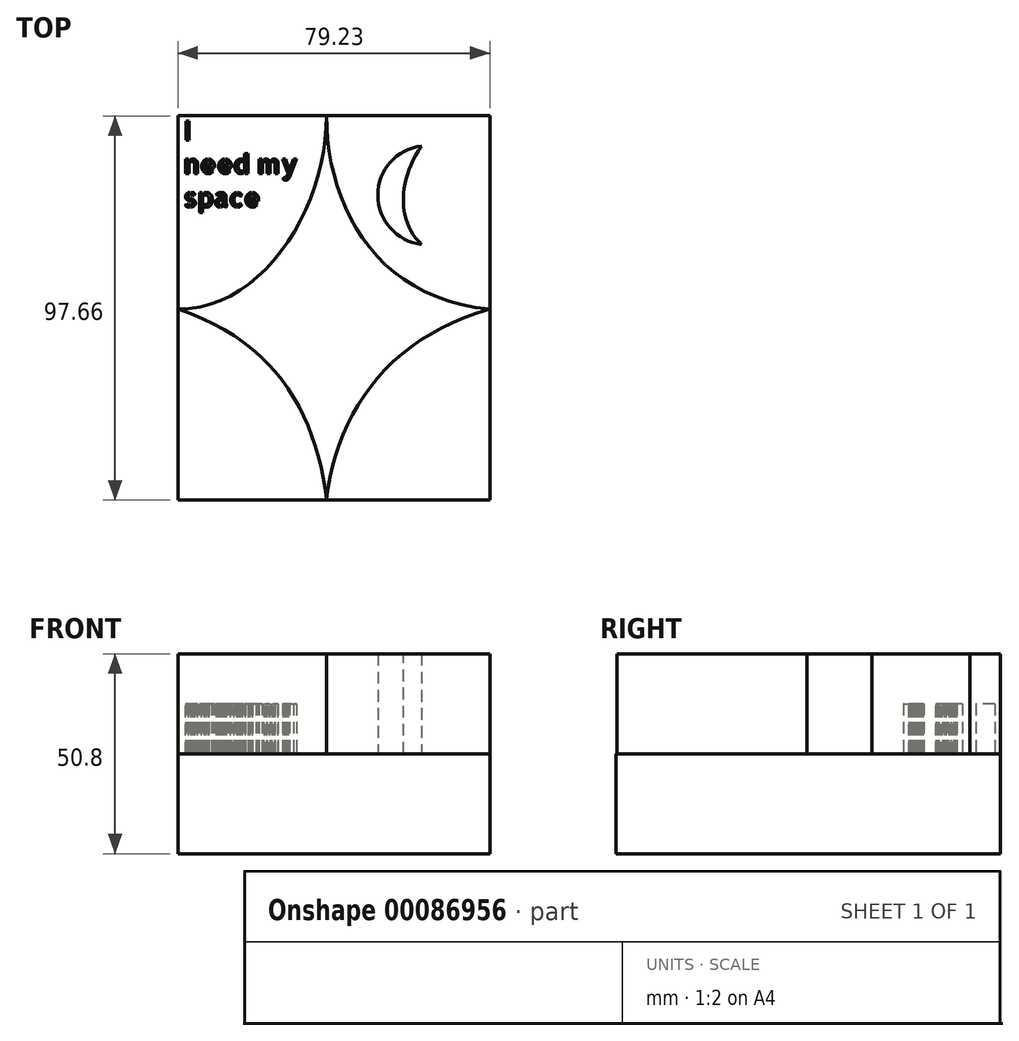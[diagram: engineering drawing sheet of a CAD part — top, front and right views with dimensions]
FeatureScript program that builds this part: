
annotation { "Feature Type Name" : "Feature", "Feature Type Description" : "" }
export const myFeature = defineFeature(function(context is Context, id is Id, definition is map)
    precondition{}
    {
        {
            var Q0;
            Q0=qCreatedBy(makeId("Top.planeOp"),FACE);
            var sketch = newSketch(context, id + "F0", { "sketchPlane" : qUnion([Q0])});
            skFitSpline(sketch, "E0", {"points": [v(-37.75, 0) * mm, v(0, 49.12) * mm], "startDerivative": vector(65.6, 0) * mm, "endDerivative": vector(-0.18, 69.09) * mm});
            skFitSpline(sketch, "E1", {"points": [v(0, 49.12) * mm, v(41.48, 0) * mm], "startDerivative": vector(0.18, -69.09) * mm, "endDerivative": vector(86.48, -7.94) * mm});
            skFitSpline(sketch, "E2", {"points": [v(41.48, 0) * mm, v(0, -48.24) * mm], "startDerivative": vector(-76.77, -21.18) * mm, "endDerivative": vector(-7.06, -65.3) * mm});
            skFitSpline(sketch, "E3", {"points": [v(-37.75, 0) * mm, v(0, -48.24) * mm], "startDerivative": vector(74.42, -24.7) * mm, "endDerivative": vector(7.94, -65.3) * mm});
            skLineSegment(sketch, "E4.bottom", {"start": v(-37.75, 49.12) * mm, "end": v(41.48, 49.12) * mm});
            skLineSegment(sketch, "E4.top", {"start": v(-37.75, -48.54) * mm, "end": v(41.48, -48.54) * mm});
            skLineSegment(sketch, "E4.left", {"start": v(-37.75, 49.12) * mm, "end": v(-37.75, -48.54) * mm});
            skLineSegment(sketch, "E4.right", {"start": v(41.48, 49.12) * mm, "end": v(41.48, -48.54) * mm});
            skSolve(sketch);
        }
        {
            var Q0;
            Q0=makeQuery(id+"F0.imprint","IMPRINT",FACE,{"disambiguationData":[TD([[makeQuery(id+"F0.imprint","IMPRINT",EDGE,{"derivedFrom":sQuery(id+"F0.wireOp",EDGE,"E0")}),-1.0]])]});
            extrude(context, id + "F1", {"entities" : qUnion([Q0]), "depth" : 50.8 * mm});
        }
        {
            var Q0;
            Q0 = qSketchRegion(id + "F0", true);
            extrude(context, id + "F2", {"entities" : qUnion([Q0]), "operationType" : NewBodyOperationType.ADD, "depth" : 25.4 * mm});
        }
        {
            var Q0;
            Q0=qCreatedBy(makeId("Top.planeOp"),FACE);
            var sketch = newSketch(context, id + "F3", { "sketchPlane" : qUnion([Q0])});
            skText(sketch, "E5", { "text": "I\nneed my\nspace", "fontName": "AllertaStencil-Regular.ttf"});
            const initialGuessF3  = {"E5": [-0.07133, 0.05854, 1, 0, 0.00478]};
            skSetInitialGuess(sketch, initialGuessF3);
            skSolve(sketch);
        }
        {
            var Q0;
            Q0 = qSketchRegion(id + "F3", true);
            extrude(context, id + "F4", {"entities" : qUnion([Q0]), "depth" : 12.7 * mm});
        }
        {
            var Q0;
            Q0=makeQuery(id+"F4.opExtrude","SWEPT_BODY",BODY,{"disambiguationData":[OSD([sQuery(id+"F3.wireOp",EDGE,"E5.sketch_text.stroke-0"),sQuery(id+"F3.wireOp",EDGE,"E5.sketch_text.stroke-1"),sQuery(id+"F3.wireOp",EDGE,"E5.sketch_text.stroke-2"),sQuery(id+"F3.wireOp",EDGE,"E5.sketch_text.stroke-3")])]});
            var Q1;
            Q1=makeQuery(id+"F4.opExtrude","SWEPT_BODY",BODY,{"disambiguationData":[OSD([sQuery(id+"F3.wireOp",EDGE,"E5.sketch_text.stroke-4"),sQuery(id+"F3.wireOp",EDGE,"E5.sketch_text.stroke-5"),sQuery(id+"F3.wireOp",EDGE,"E5.sketch_text.stroke-6"),sQuery(id+"F3.wireOp",EDGE,"E5.sketch_text.stroke-7"),sQuery(id+"F3.wireOp",EDGE,"E5.sketch_text.stroke-8")])]});
            var Q2;
            Q2=makeQuery(id+"F4.opExtrude","SWEPT_BODY",BODY,{"disambiguationData":[OSD([sQuery(id+"F3.wireOp",EDGE,"E5.sketch_text.stroke-9"),sQuery(id+"F3.wireOp",EDGE,"E5.sketch_text.stroke-10"),sQuery(id+"F3.wireOp",EDGE,"E5.sketch_text.stroke-11"),sQuery(id+"F3.wireOp",EDGE,"E5.sketch_text.stroke-12"),sQuery(id+"F3.wireOp",EDGE,"E5.sketch_text.stroke-13"),sQuery(id+"F3.wireOp",EDGE,"E5.sketch_text.stroke-14"),sQuery(id+"F3.wireOp",EDGE,"E5.sketch_text.stroke-15"),sQuery(id+"F3.wireOp",EDGE,"E5.sketch_text.stroke-16"),sQuery(id+"F3.wireOp",EDGE,"E5.sketch_text.stroke-17"),sQuery(id+"F3.wireOp",EDGE,"E5.sketch_text.stroke-18"),sQuery(id+"F3.wireOp",EDGE,"E5.sketch_text.stroke-19"),sQuery(id+"F3.wireOp",EDGE,"E5.sketch_text.stroke-20"),sQuery(id+"F3.wireOp",EDGE,"E5.sketch_text.stroke-21"),sQuery(id+"F3.wireOp",EDGE,"E5.sketch_text.stroke-22"),sQuery(id+"F3.wireOp",EDGE,"E5.sketch_text.stroke-23"),sQuery(id+"F3.wireOp",EDGE,"E5.sketch_text.stroke-24"),sQuery(id+"F3.wireOp",EDGE,"E5.sketch_text.stroke-25"),sQuery(id+"F3.wireOp",EDGE,"E5.sketch_text.stroke-26"),sQuery(id+"F3.wireOp",EDGE,"E5.sketch_text.stroke-27")])]});
            var Q3;
            Q3=makeQuery(id+"F4.opExtrude","SWEPT_BODY",BODY,{"disambiguationData":[OSD([sQuery(id+"F3.wireOp",EDGE,"E5.sketch_text.stroke-28"),sQuery(id+"F3.wireOp",EDGE,"E5.sketch_text.stroke-29"),sQuery(id+"F3.wireOp",EDGE,"E5.sketch_text.stroke-30"),sQuery(id+"F3.wireOp",EDGE,"E5.sketch_text.stroke-31"),sQuery(id+"F3.wireOp",EDGE,"E5.sketch_text.stroke-32"),sQuery(id+"F3.wireOp",EDGE,"E5.sketch_text.stroke-33"),sQuery(id+"F3.wireOp",EDGE,"E5.sketch_text.stroke-34"),sQuery(id+"F3.wireOp",EDGE,"E5.sketch_text.stroke-35"),sQuery(id+"F3.wireOp",EDGE,"E5.sketch_text.stroke-36"),sQuery(id+"F3.wireOp",EDGE,"E5.sketch_text.stroke-37"),sQuery(id+"F3.wireOp",EDGE,"E5.sketch_text.stroke-38"),sQuery(id+"F3.wireOp",EDGE,"E5.sketch_text.stroke-39"),sQuery(id+"F3.wireOp",EDGE,"E5.sketch_text.stroke-40")])]});
            var Q4;
            Q4=makeQuery(id+"F4.opExtrude","SWEPT_BODY",BODY,{"disambiguationData":[OSD([sQuery(id+"F3.wireOp",EDGE,"E5.sketch_text.stroke-41"),sQuery(id+"F3.wireOp",EDGE,"E5.sketch_text.stroke-42"),sQuery(id+"F3.wireOp",EDGE,"E5.sketch_text.stroke-43"),sQuery(id+"F3.wireOp",EDGE,"E5.sketch_text.stroke-44"),sQuery(id+"F3.wireOp",EDGE,"E5.sketch_text.stroke-45"),sQuery(id+"F3.wireOp",EDGE,"E5.sketch_text.stroke-46"),sQuery(id+"F3.wireOp",EDGE,"E5.sketch_text.stroke-47"),sQuery(id+"F3.wireOp",EDGE,"E5.sketch_text.stroke-48"),sQuery(id+"F3.wireOp",EDGE,"E5.sketch_text.stroke-49"),sQuery(id+"F3.wireOp",EDGE,"E5.sketch_text.stroke-50"),sQuery(id+"F3.wireOp",EDGE,"E5.sketch_text.stroke-51"),sQuery(id+"F3.wireOp",EDGE,"E5.sketch_text.stroke-52"),sQuery(id+"F3.wireOp",EDGE,"E5.sketch_text.stroke-53"),sQuery(id+"F3.wireOp",EDGE,"E5.sketch_text.stroke-54"),sQuery(id+"F3.wireOp",EDGE,"E5.sketch_text.stroke-55"),sQuery(id+"F3.wireOp",EDGE,"E5.sketch_text.stroke-56"),sQuery(id+"F3.wireOp",EDGE,"E5.sketch_text.stroke-57"),sQuery(id+"F3.wireOp",EDGE,"E5.sketch_text.stroke-58"),sQuery(id+"F3.wireOp",EDGE,"E5.sketch_text.stroke-59"),sQuery(id+"F3.wireOp",EDGE,"E5.sketch_text.stroke-60"),sQuery(id+"F3.wireOp",EDGE,"E5.sketch_text.stroke-61"),sQuery(id+"F3.wireOp",EDGE,"E5.sketch_text.stroke-62"),sQuery(id+"F3.wireOp",EDGE,"E5.sketch_text.stroke-63"),sQuery(id+"F3.wireOp",EDGE,"E5.sketch_text.stroke-64")])]});
            var Q5;
            Q5=makeQuery(id+"F4.opExtrude","SWEPT_BODY",BODY,{"disambiguationData":[OSD([sQuery(id+"F3.wireOp",EDGE,"E5.sketch_text.stroke-65"),sQuery(id+"F3.wireOp",EDGE,"E5.sketch_text.stroke-66"),sQuery(id+"F3.wireOp",EDGE,"E5.sketch_text.stroke-67"),sQuery(id+"F3.wireOp",EDGE,"E5.sketch_text.stroke-68"),sQuery(id+"F3.wireOp",EDGE,"E5.sketch_text.stroke-69"),sQuery(id+"F3.wireOp",EDGE,"E5.sketch_text.stroke-70"),sQuery(id+"F3.wireOp",EDGE,"E5.sketch_text.stroke-71"),sQuery(id+"F3.wireOp",EDGE,"E5.sketch_text.stroke-72"),sQuery(id+"F3.wireOp",EDGE,"E5.sketch_text.stroke-73"),sQuery(id+"F3.wireOp",EDGE,"E5.sketch_text.stroke-74"),sQuery(id+"F3.wireOp",EDGE,"E5.sketch_text.stroke-75"),sQuery(id+"F3.wireOp",EDGE,"E5.sketch_text.stroke-76"),sQuery(id+"F3.wireOp",EDGE,"E5.sketch_text.stroke-77")])]});
            var Q6;
            Q6=makeQuery(id+"F4.opExtrude","SWEPT_BODY",BODY,{"disambiguationData":[OSD([sQuery(id+"F3.wireOp",EDGE,"E5.sketch_text.stroke-78"),sQuery(id+"F3.wireOp",EDGE,"E5.sketch_text.stroke-79"),sQuery(id+"F3.wireOp",EDGE,"E5.sketch_text.stroke-80"),sQuery(id+"F3.wireOp",EDGE,"E5.sketch_text.stroke-81"),sQuery(id+"F3.wireOp",EDGE,"E5.sketch_text.stroke-82"),sQuery(id+"F3.wireOp",EDGE,"E5.sketch_text.stroke-83"),sQuery(id+"F3.wireOp",EDGE,"E5.sketch_text.stroke-84"),sQuery(id+"F3.wireOp",EDGE,"E5.sketch_text.stroke-85"),sQuery(id+"F3.wireOp",EDGE,"E5.sketch_text.stroke-86"),sQuery(id+"F3.wireOp",EDGE,"E5.sketch_text.stroke-87"),sQuery(id+"F3.wireOp",EDGE,"E5.sketch_text.stroke-88"),sQuery(id+"F3.wireOp",EDGE,"E5.sketch_text.stroke-89"),sQuery(id+"F3.wireOp",EDGE,"E5.sketch_text.stroke-90"),sQuery(id+"F3.wireOp",EDGE,"E5.sketch_text.stroke-91"),sQuery(id+"F3.wireOp",EDGE,"E5.sketch_text.stroke-92"),sQuery(id+"F3.wireOp",EDGE,"E5.sketch_text.stroke-93"),sQuery(id+"F3.wireOp",EDGE,"E5.sketch_text.stroke-94"),sQuery(id+"F3.wireOp",EDGE,"E5.sketch_text.stroke-95"),sQuery(id+"F3.wireOp",EDGE,"E5.sketch_text.stroke-96"),sQuery(id+"F3.wireOp",EDGE,"E5.sketch_text.stroke-97"),sQuery(id+"F3.wireOp",EDGE,"E5.sketch_text.stroke-98"),sQuery(id+"F3.wireOp",EDGE,"E5.sketch_text.stroke-99"),sQuery(id+"F3.wireOp",EDGE,"E5.sketch_text.stroke-100"),sQuery(id+"F3.wireOp",EDGE,"E5.sketch_text.stroke-101")])]});
            var Q7;
            Q7=makeQuery(id+"F4.opExtrude","SWEPT_BODY",BODY,{"disambiguationData":[OSD([sQuery(id+"F3.wireOp",EDGE,"E5.sketch_text.stroke-102"),sQuery(id+"F3.wireOp",EDGE,"E5.sketch_text.stroke-103"),sQuery(id+"F3.wireOp",EDGE,"E5.sketch_text.stroke-104"),sQuery(id+"F3.wireOp",EDGE,"E5.sketch_text.stroke-105"),sQuery(id+"F3.wireOp",EDGE,"E5.sketch_text.stroke-106")])]});
            var Q8;
            Q8=makeQuery(id+"F4.opExtrude","SWEPT_BODY",BODY,{"disambiguationData":[OSD([sQuery(id+"F3.wireOp",EDGE,"E5.sketch_text.stroke-107"),sQuery(id+"F3.wireOp",EDGE,"E5.sketch_text.stroke-108"),sQuery(id+"F3.wireOp",EDGE,"E5.sketch_text.stroke-109"),sQuery(id+"F3.wireOp",EDGE,"E5.sketch_text.stroke-110"),sQuery(id+"F3.wireOp",EDGE,"E5.sketch_text.stroke-111"),sQuery(id+"F3.wireOp",EDGE,"E5.sketch_text.stroke-112"),sQuery(id+"F3.wireOp",EDGE,"E5.sketch_text.stroke-113"),sQuery(id+"F3.wireOp",EDGE,"E5.sketch_text.stroke-114"),sQuery(id+"F3.wireOp",EDGE,"E5.sketch_text.stroke-115"),sQuery(id+"F3.wireOp",EDGE,"E5.sketch_text.stroke-116"),sQuery(id+"F3.wireOp",EDGE,"E5.sketch_text.stroke-117"),sQuery(id+"F3.wireOp",EDGE,"E5.sketch_text.stroke-118"),sQuery(id+"F3.wireOp",EDGE,"E5.sketch_text.stroke-119"),sQuery(id+"F3.wireOp",EDGE,"E5.sketch_text.stroke-120"),sQuery(id+"F3.wireOp",EDGE,"E5.sketch_text.stroke-121"),sQuery(id+"F3.wireOp",EDGE,"E5.sketch_text.stroke-122"),sQuery(id+"F3.wireOp",EDGE,"E5.sketch_text.stroke-123"),sQuery(id+"F3.wireOp",EDGE,"E5.sketch_text.stroke-124"),sQuery(id+"F3.wireOp",EDGE,"E5.sketch_text.stroke-125"),sQuery(id+"F3.wireOp",EDGE,"E5.sketch_text.stroke-126"),sQuery(id+"F3.wireOp",EDGE,"E5.sketch_text.stroke-127"),sQuery(id+"F3.wireOp",EDGE,"E5.sketch_text.stroke-128"),sQuery(id+"F3.wireOp",EDGE,"E5.sketch_text.stroke-129"),sQuery(id+"F3.wireOp",EDGE,"E5.sketch_text.stroke-130"),sQuery(id+"F3.wireOp",EDGE,"E5.sketch_text.stroke-131")])]});
            var Q9;
            Q9=makeQuery(id+"F4.opExtrude","SWEPT_BODY",BODY,{"disambiguationData":[OSD([sQuery(id+"F3.wireOp",EDGE,"E5.sketch_text.stroke-132"),sQuery(id+"F3.wireOp",EDGE,"E5.sketch_text.stroke-133"),sQuery(id+"F3.wireOp",EDGE,"E5.sketch_text.stroke-134"),sQuery(id+"F3.wireOp",EDGE,"E5.sketch_text.stroke-135"),sQuery(id+"F3.wireOp",EDGE,"E5.sketch_text.stroke-136")])]});
            var Q10;
            Q10=makeQuery(id+"F4.opExtrude","SWEPT_BODY",BODY,{"disambiguationData":[OSD([sQuery(id+"F3.wireOp",EDGE,"E5.sketch_text.stroke-137"),sQuery(id+"F3.wireOp",EDGE,"E5.sketch_text.stroke-138"),sQuery(id+"F3.wireOp",EDGE,"E5.sketch_text.stroke-139"),sQuery(id+"F3.wireOp",EDGE,"E5.sketch_text.stroke-140"),sQuery(id+"F3.wireOp",EDGE,"E5.sketch_text.stroke-141"),sQuery(id+"F3.wireOp",EDGE,"E5.sketch_text.stroke-142"),sQuery(id+"F3.wireOp",EDGE,"E5.sketch_text.stroke-143"),sQuery(id+"F3.wireOp",EDGE,"E5.sketch_text.stroke-144"),sQuery(id+"F3.wireOp",EDGE,"E5.sketch_text.stroke-145"),sQuery(id+"F3.wireOp",EDGE,"E5.sketch_text.stroke-146"),sQuery(id+"F3.wireOp",EDGE,"E5.sketch_text.stroke-147"),sQuery(id+"F3.wireOp",EDGE,"E5.sketch_text.stroke-148"),sQuery(id+"F3.wireOp",EDGE,"E5.sketch_text.stroke-149"),sQuery(id+"F3.wireOp",EDGE,"E5.sketch_text.stroke-150"),sQuery(id+"F3.wireOp",EDGE,"E5.sketch_text.stroke-151"),sQuery(id+"F3.wireOp",EDGE,"E5.sketch_text.stroke-152")])]});
            var Q11;
            Q11=makeQuery(id+"F4.opExtrude","SWEPT_BODY",BODY,{"disambiguationData":[OSD([sQuery(id+"F3.wireOp",EDGE,"E5.sketch_text.stroke-153"),sQuery(id+"F3.wireOp",EDGE,"E5.sketch_text.stroke-154"),sQuery(id+"F3.wireOp",EDGE,"E5.sketch_text.stroke-155"),sQuery(id+"F3.wireOp",EDGE,"E5.sketch_text.stroke-156"),sQuery(id+"F3.wireOp",EDGE,"E5.sketch_text.stroke-157"),sQuery(id+"F3.wireOp",EDGE,"E5.sketch_text.stroke-158"),sQuery(id+"F3.wireOp",EDGE,"E5.sketch_text.stroke-159"),sQuery(id+"F3.wireOp",EDGE,"E5.sketch_text.stroke-160"),sQuery(id+"F3.wireOp",EDGE,"E5.sketch_text.stroke-161"),sQuery(id+"F3.wireOp",EDGE,"E5.sketch_text.stroke-162"),sQuery(id+"F3.wireOp",EDGE,"E5.sketch_text.stroke-163"),sQuery(id+"F3.wireOp",EDGE,"E5.sketch_text.stroke-164"),sQuery(id+"F3.wireOp",EDGE,"E5.sketch_text.stroke-165"),sQuery(id+"F3.wireOp",EDGE,"E5.sketch_text.stroke-166"),sQuery(id+"F3.wireOp",EDGE,"E5.sketch_text.stroke-167"),sQuery(id+"F3.wireOp",EDGE,"E5.sketch_text.stroke-168"),sQuery(id+"F3.wireOp",EDGE,"E5.sketch_text.stroke-169"),sQuery(id+"F3.wireOp",EDGE,"E5.sketch_text.stroke-170")])]});
            var Q12;
            Q12=makeQuery(id+"F4.opExtrude","SWEPT_BODY",BODY,{"disambiguationData":[OSD([sQuery(id+"F3.wireOp",EDGE,"E5.sketch_text.stroke-171"),sQuery(id+"F3.wireOp",EDGE,"E5.sketch_text.stroke-172"),sQuery(id+"F3.wireOp",EDGE,"E5.sketch_text.stroke-173"),sQuery(id+"F3.wireOp",EDGE,"E5.sketch_text.stroke-174"),sQuery(id+"F3.wireOp",EDGE,"E5.sketch_text.stroke-175"),sQuery(id+"F3.wireOp",EDGE,"E5.sketch_text.stroke-176"),sQuery(id+"F3.wireOp",EDGE,"E5.sketch_text.stroke-177"),sQuery(id+"F3.wireOp",EDGE,"E5.sketch_text.stroke-178"),sQuery(id+"F3.wireOp",EDGE,"E5.sketch_text.stroke-179"),sQuery(id+"F3.wireOp",EDGE,"E5.sketch_text.stroke-180"),sQuery(id+"F3.wireOp",EDGE,"E5.sketch_text.stroke-181"),sQuery(id+"F3.wireOp",EDGE,"E5.sketch_text.stroke-182"),sQuery(id+"F3.wireOp",EDGE,"E5.sketch_text.stroke-183"),sQuery(id+"F3.wireOp",EDGE,"E5.sketch_text.stroke-184"),sQuery(id+"F3.wireOp",EDGE,"E5.sketch_text.stroke-185"),sQuery(id+"F3.wireOp",EDGE,"E5.sketch_text.stroke-186"),sQuery(id+"F3.wireOp",EDGE,"E5.sketch_text.stroke-187"),sQuery(id+"F3.wireOp",EDGE,"E5.sketch_text.stroke-188"),sQuery(id+"F3.wireOp",EDGE,"E5.sketch_text.stroke-189"),sQuery(id+"F3.wireOp",EDGE,"E5.sketch_text.stroke-190"),sQuery(id+"F3.wireOp",EDGE,"E5.sketch_text.stroke-191"),sQuery(id+"F3.wireOp",EDGE,"E5.sketch_text.stroke-192"),sQuery(id+"F3.wireOp",EDGE,"E5.sketch_text.stroke-193"),sQuery(id+"F3.wireOp",EDGE,"E5.sketch_text.stroke-194")])]});
            var Q13;
            Q13=makeQuery(id+"F4.opExtrude","SWEPT_BODY",BODY,{"disambiguationData":[OSD([sQuery(id+"F3.wireOp",EDGE,"E5.sketch_text.stroke-195"),sQuery(id+"F3.wireOp",EDGE,"E5.sketch_text.stroke-196"),sQuery(id+"F3.wireOp",EDGE,"E5.sketch_text.stroke-197"),sQuery(id+"F3.wireOp",EDGE,"E5.sketch_text.stroke-198"),sQuery(id+"F3.wireOp",EDGE,"E5.sketch_text.stroke-199")])]});
            var Q14;
            Q14=makeQuery(id+"F4.opExtrude","SWEPT_BODY",BODY,{"disambiguationData":[OSD([sQuery(id+"F3.wireOp",EDGE,"E5.sketch_text.stroke-200"),sQuery(id+"F3.wireOp",EDGE,"E5.sketch_text.stroke-201"),sQuery(id+"F3.wireOp",EDGE,"E5.sketch_text.stroke-202"),sQuery(id+"F3.wireOp",EDGE,"E5.sketch_text.stroke-203"),sQuery(id+"F3.wireOp",EDGE,"E5.sketch_text.stroke-204"),sQuery(id+"F3.wireOp",EDGE,"E5.sketch_text.stroke-205"),sQuery(id+"F3.wireOp",EDGE,"E5.sketch_text.stroke-206"),sQuery(id+"F3.wireOp",EDGE,"E5.sketch_text.stroke-207"),sQuery(id+"F3.wireOp",EDGE,"E5.sketch_text.stroke-208"),sQuery(id+"F3.wireOp",EDGE,"E5.sketch_text.stroke-209"),sQuery(id+"F3.wireOp",EDGE,"E5.sketch_text.stroke-210"),sQuery(id+"F3.wireOp",EDGE,"E5.sketch_text.stroke-211"),sQuery(id+"F3.wireOp",EDGE,"E5.sketch_text.stroke-212"),sQuery(id+"F3.wireOp",EDGE,"E5.sketch_text.stroke-213")])]});
            var Q15;
            Q15=makeQuery(id+"F4.opExtrude","SWEPT_BODY",BODY,{"disambiguationData":[OSD([sQuery(id+"F3.wireOp",EDGE,"E5.sketch_text.stroke-214"),sQuery(id+"F3.wireOp",EDGE,"E5.sketch_text.stroke-215"),sQuery(id+"F3.wireOp",EDGE,"E5.sketch_text.stroke-216"),sQuery(id+"F3.wireOp",EDGE,"E5.sketch_text.stroke-217"),sQuery(id+"F3.wireOp",EDGE,"E5.sketch_text.stroke-218"),sQuery(id+"F3.wireOp",EDGE,"E5.sketch_text.stroke-219")])]});
            var Q16;
            Q16=makeQuery(id+"F4.opExtrude","SWEPT_BODY",BODY,{"disambiguationData":[OSD([sQuery(id+"F3.wireOp",EDGE,"E5.sketch_text.stroke-220"),sQuery(id+"F3.wireOp",EDGE,"E5.sketch_text.stroke-221"),sQuery(id+"F3.wireOp",EDGE,"E5.sketch_text.stroke-222"),sQuery(id+"F3.wireOp",EDGE,"E5.sketch_text.stroke-223"),sQuery(id+"F3.wireOp",EDGE,"E5.sketch_text.stroke-224"),sQuery(id+"F3.wireOp",EDGE,"E5.sketch_text.stroke-225"),sQuery(id+"F3.wireOp",EDGE,"E5.sketch_text.stroke-226"),sQuery(id+"F3.wireOp",EDGE,"E5.sketch_text.stroke-227"),sQuery(id+"F3.wireOp",EDGE,"E5.sketch_text.stroke-228")])]});
            var Q17;
            Q17=makeQuery(id+"F4.opExtrude","SWEPT_BODY",BODY,{"disambiguationData":[OSD([sQuery(id+"F3.wireOp",EDGE,"E5.sketch_text.stroke-229"),sQuery(id+"F3.wireOp",EDGE,"E5.sketch_text.stroke-230"),sQuery(id+"F3.wireOp",EDGE,"E5.sketch_text.stroke-231"),sQuery(id+"F3.wireOp",EDGE,"E5.sketch_text.stroke-232"),sQuery(id+"F3.wireOp",EDGE,"E5.sketch_text.stroke-233"),sQuery(id+"F3.wireOp",EDGE,"E5.sketch_text.stroke-234"),sQuery(id+"F3.wireOp",EDGE,"E5.sketch_text.stroke-235"),sQuery(id+"F3.wireOp",EDGE,"E5.sketch_text.stroke-236"),sQuery(id+"F3.wireOp",EDGE,"E5.sketch_text.stroke-237"),sQuery(id+"F3.wireOp",EDGE,"E5.sketch_text.stroke-238"),sQuery(id+"F3.wireOp",EDGE,"E5.sketch_text.stroke-239"),sQuery(id+"F3.wireOp",EDGE,"E5.sketch_text.stroke-240"),sQuery(id+"F3.wireOp",EDGE,"E5.sketch_text.stroke-241"),sQuery(id+"F3.wireOp",EDGE,"E5.sketch_text.stroke-242")])]});
            var Q18;
            Q18=makeQuery(id+"F4.opExtrude","SWEPT_BODY",BODY,{"disambiguationData":[OSD([sQuery(id+"F3.wireOp",EDGE,"E5.sketch_text.stroke-243"),sQuery(id+"F3.wireOp",EDGE,"E5.sketch_text.stroke-244"),sQuery(id+"F3.wireOp",EDGE,"E5.sketch_text.stroke-245"),sQuery(id+"F3.wireOp",EDGE,"E5.sketch_text.stroke-246"),sQuery(id+"F3.wireOp",EDGE,"E5.sketch_text.stroke-247")])]});
            var Q19;
            Q19=makeQuery(id+"F4.opExtrude","SWEPT_BODY",BODY,{"disambiguationData":[OSD([sQuery(id+"F3.wireOp",EDGE,"E5.sketch_text.stroke-248"),sQuery(id+"F3.wireOp",EDGE,"E5.sketch_text.stroke-249"),sQuery(id+"F3.wireOp",EDGE,"E5.sketch_text.stroke-250"),sQuery(id+"F3.wireOp",EDGE,"E5.sketch_text.stroke-251"),sQuery(id+"F3.wireOp",EDGE,"E5.sketch_text.stroke-252"),sQuery(id+"F3.wireOp",EDGE,"E5.sketch_text.stroke-253"),sQuery(id+"F3.wireOp",EDGE,"E5.sketch_text.stroke-254"),sQuery(id+"F3.wireOp",EDGE,"E5.sketch_text.stroke-255"),sQuery(id+"F3.wireOp",EDGE,"E5.sketch_text.stroke-256"),sQuery(id+"F3.wireOp",EDGE,"E5.sketch_text.stroke-257"),sQuery(id+"F3.wireOp",EDGE,"E5.sketch_text.stroke-258"),sQuery(id+"F3.wireOp",EDGE,"E5.sketch_text.stroke-259"),sQuery(id+"F3.wireOp",EDGE,"E5.sketch_text.stroke-260"),sQuery(id+"F3.wireOp",EDGE,"E5.sketch_text.stroke-261"),sQuery(id+"F3.wireOp",EDGE,"E5.sketch_text.stroke-262"),sQuery(id+"F3.wireOp",EDGE,"E5.sketch_text.stroke-263"),sQuery(id+"F3.wireOp",EDGE,"E5.sketch_text.stroke-264"),sQuery(id+"F3.wireOp",EDGE,"E5.sketch_text.stroke-265"),sQuery(id+"F3.wireOp",EDGE,"E5.sketch_text.stroke-266"),sQuery(id+"F3.wireOp",EDGE,"E5.sketch_text.stroke-267"),sQuery(id+"F3.wireOp",EDGE,"E5.sketch_text.stroke-268"),sQuery(id+"F3.wireOp",EDGE,"E5.sketch_text.stroke-269"),sQuery(id+"F3.wireOp",EDGE,"E5.sketch_text.stroke-270"),sQuery(id+"F3.wireOp",EDGE,"E5.sketch_text.stroke-271"),sQuery(id+"F3.wireOp",EDGE,"E5.sketch_text.stroke-272"),sQuery(id+"F3.wireOp",EDGE,"E5.sketch_text.stroke-273")])]});
            var Q20;
            Q20=makeQuery(id+"F4.opExtrude","SWEPT_BODY",BODY,{"disambiguationData":[OSD([sQuery(id+"F3.wireOp",EDGE,"E5.sketch_text.stroke-274"),sQuery(id+"F3.wireOp",EDGE,"E5.sketch_text.stroke-275"),sQuery(id+"F3.wireOp",EDGE,"E5.sketch_text.stroke-276"),sQuery(id+"F3.wireOp",EDGE,"E5.sketch_text.stroke-277"),sQuery(id+"F3.wireOp",EDGE,"E5.sketch_text.stroke-278"),sQuery(id+"F3.wireOp",EDGE,"E5.sketch_text.stroke-279"),sQuery(id+"F3.wireOp",EDGE,"E5.sketch_text.stroke-280"),sQuery(id+"F3.wireOp",EDGE,"E5.sketch_text.stroke-281"),sQuery(id+"F3.wireOp",EDGE,"E5.sketch_text.stroke-282"),sQuery(id+"F3.wireOp",EDGE,"E5.sketch_text.stroke-283"),sQuery(id+"F3.wireOp",EDGE,"E5.sketch_text.stroke-284"),sQuery(id+"F3.wireOp",EDGE,"E5.sketch_text.stroke-285"),sQuery(id+"F3.wireOp",EDGE,"E5.sketch_text.stroke-286"),sQuery(id+"F3.wireOp",EDGE,"E5.sketch_text.stroke-287"),sQuery(id+"F3.wireOp",EDGE,"E5.sketch_text.stroke-288"),sQuery(id+"F3.wireOp",EDGE,"E5.sketch_text.stroke-289"),sQuery(id+"F3.wireOp",EDGE,"E5.sketch_text.stroke-290"),sQuery(id+"F3.wireOp",EDGE,"E5.sketch_text.stroke-291"),sQuery(id+"F3.wireOp",EDGE,"E5.sketch_text.stroke-292")])]});
            var Q21;
            Q21=makeQuery(id+"F4.opExtrude","SWEPT_BODY",BODY,{"disambiguationData":[OSD([sQuery(id+"F3.wireOp",EDGE,"E5.sketch_text.stroke-293"),sQuery(id+"F3.wireOp",EDGE,"E5.sketch_text.stroke-294"),sQuery(id+"F3.wireOp",EDGE,"E5.sketch_text.stroke-295"),sQuery(id+"F3.wireOp",EDGE,"E5.sketch_text.stroke-296"),sQuery(id+"F3.wireOp",EDGE,"E5.sketch_text.stroke-297"),sQuery(id+"F3.wireOp",EDGE,"E5.sketch_text.stroke-298"),sQuery(id+"F3.wireOp",EDGE,"E5.sketch_text.stroke-299"),sQuery(id+"F3.wireOp",EDGE,"E5.sketch_text.stroke-300"),sQuery(id+"F3.wireOp",EDGE,"E5.sketch_text.stroke-301"),sQuery(id+"F3.wireOp",EDGE,"E5.sketch_text.stroke-302"),sQuery(id+"F3.wireOp",EDGE,"E5.sketch_text.stroke-303"),sQuery(id+"F3.wireOp",EDGE,"E5.sketch_text.stroke-304"),sQuery(id+"F3.wireOp",EDGE,"E5.sketch_text.stroke-305"),sQuery(id+"F3.wireOp",EDGE,"E5.sketch_text.stroke-306"),sQuery(id+"F3.wireOp",EDGE,"E5.sketch_text.stroke-307"),sQuery(id+"F3.wireOp",EDGE,"E5.sketch_text.stroke-308"),sQuery(id+"F3.wireOp",EDGE,"E5.sketch_text.stroke-309"),sQuery(id+"F3.wireOp",EDGE,"E5.sketch_text.stroke-310"),sQuery(id+"F3.wireOp",EDGE,"E5.sketch_text.stroke-311"),sQuery(id+"F3.wireOp",EDGE,"E5.sketch_text.stroke-312"),sQuery(id+"F3.wireOp",EDGE,"E5.sketch_text.stroke-313"),sQuery(id+"F3.wireOp",EDGE,"E5.sketch_text.stroke-314"),sQuery(id+"F3.wireOp",EDGE,"E5.sketch_text.stroke-315"),sQuery(id+"F3.wireOp",EDGE,"E5.sketch_text.stroke-316"),sQuery(id+"F3.wireOp",EDGE,"E5.sketch_text.stroke-317"),sQuery(id+"F3.wireOp",EDGE,"E5.sketch_text.stroke-318"),sQuery(id+"F3.wireOp",EDGE,"E5.sketch_text.stroke-319"),sQuery(id+"F3.wireOp",EDGE,"E5.sketch_text.stroke-320"),sQuery(id+"F3.wireOp",EDGE,"E5.sketch_text.stroke-321"),sQuery(id+"F3.wireOp",EDGE,"E5.sketch_text.stroke-322"),sQuery(id+"F3.wireOp",EDGE,"E5.sketch_text.stroke-323"),sQuery(id+"F3.wireOp",EDGE,"E5.sketch_text.stroke-324"),sQuery(id+"F3.wireOp",EDGE,"E5.sketch_text.stroke-325"),sQuery(id+"F3.wireOp",EDGE,"E5.sketch_text.stroke-326"),sQuery(id+"F3.wireOp",EDGE,"E5.sketch_text.stroke-327"),sQuery(id+"F3.wireOp",EDGE,"E5.sketch_text.stroke-328")])]});
            var Q22;
            Q22=makeQuery(id+"F4.opExtrude","SWEPT_BODY",BODY,{"disambiguationData":[OSD([sQuery(id+"F3.wireOp",EDGE,"E5.sketch_text.stroke-329"),sQuery(id+"F3.wireOp",EDGE,"E5.sketch_text.stroke-330"),sQuery(id+"F3.wireOp",EDGE,"E5.sketch_text.stroke-331"),sQuery(id+"F3.wireOp",EDGE,"E5.sketch_text.stroke-332"),sQuery(id+"F3.wireOp",EDGE,"E5.sketch_text.stroke-333"),sQuery(id+"F3.wireOp",EDGE,"E5.sketch_text.stroke-334")])]});
            var Q23;
            Q23=makeQuery(id+"F4.opExtrude","SWEPT_BODY",BODY,{"disambiguationData":[OSD([sQuery(id+"F3.wireOp",EDGE,"E5.sketch_text.stroke-335"),sQuery(id+"F3.wireOp",EDGE,"E5.sketch_text.stroke-336"),sQuery(id+"F3.wireOp",EDGE,"E5.sketch_text.stroke-337"),sQuery(id+"F3.wireOp",EDGE,"E5.sketch_text.stroke-338"),sQuery(id+"F3.wireOp",EDGE,"E5.sketch_text.stroke-339"),sQuery(id+"F3.wireOp",EDGE,"E5.sketch_text.stroke-340")])]});
            var Q24;
            Q24=makeQuery(id+"F4.opExtrude","SWEPT_BODY",BODY,{"disambiguationData":[OSD([sQuery(id+"F3.wireOp",EDGE,"E5.sketch_text.stroke-341"),sQuery(id+"F3.wireOp",EDGE,"E5.sketch_text.stroke-342"),sQuery(id+"F3.wireOp",EDGE,"E5.sketch_text.stroke-343"),sQuery(id+"F3.wireOp",EDGE,"E5.sketch_text.stroke-344"),sQuery(id+"F3.wireOp",EDGE,"E5.sketch_text.stroke-345"),sQuery(id+"F3.wireOp",EDGE,"E5.sketch_text.stroke-346"),sQuery(id+"F3.wireOp",EDGE,"E5.sketch_text.stroke-347"),sQuery(id+"F3.wireOp",EDGE,"E5.sketch_text.stroke-348"),sQuery(id+"F3.wireOp",EDGE,"E5.sketch_text.stroke-349"),sQuery(id+"F3.wireOp",EDGE,"E5.sketch_text.stroke-350"),sQuery(id+"F3.wireOp",EDGE,"E5.sketch_text.stroke-351"),sQuery(id+"F3.wireOp",EDGE,"E5.sketch_text.stroke-352"),sQuery(id+"F3.wireOp",EDGE,"E5.sketch_text.stroke-353"),sQuery(id+"F3.wireOp",EDGE,"E5.sketch_text.stroke-354"),sQuery(id+"F3.wireOp",EDGE,"E5.sketch_text.stroke-355"),sQuery(id+"F3.wireOp",EDGE,"E5.sketch_text.stroke-356")])]});
            var Q25;
            Q25=makeQuery(id+"F4.opExtrude","SWEPT_BODY",BODY,{"disambiguationData":[OSD([sQuery(id+"F3.wireOp",EDGE,"E5.sketch_text.stroke-357"),sQuery(id+"F3.wireOp",EDGE,"E5.sketch_text.stroke-358"),sQuery(id+"F3.wireOp",EDGE,"E5.sketch_text.stroke-359"),sQuery(id+"F3.wireOp",EDGE,"E5.sketch_text.stroke-360"),sQuery(id+"F3.wireOp",EDGE,"E5.sketch_text.stroke-361"),sQuery(id+"F3.wireOp",EDGE,"E5.sketch_text.stroke-362"),sQuery(id+"F3.wireOp",EDGE,"E5.sketch_text.stroke-363"),sQuery(id+"F3.wireOp",EDGE,"E5.sketch_text.stroke-364"),sQuery(id+"F3.wireOp",EDGE,"E5.sketch_text.stroke-365"),sQuery(id+"F3.wireOp",EDGE,"E5.sketch_text.stroke-366"),sQuery(id+"F3.wireOp",EDGE,"E5.sketch_text.stroke-367"),sQuery(id+"F3.wireOp",EDGE,"E5.sketch_text.stroke-368"),sQuery(id+"F3.wireOp",EDGE,"E5.sketch_text.stroke-369")])]});
            var Q26;
            Q26=makeQuery(id+"F4.opExtrude","SWEPT_BODY",BODY,{"disambiguationData":[OSD([sQuery(id+"F3.wireOp",EDGE,"E5.sketch_text.stroke-370"),sQuery(id+"F3.wireOp",EDGE,"E5.sketch_text.stroke-371"),sQuery(id+"F3.wireOp",EDGE,"E5.sketch_text.stroke-372"),sQuery(id+"F3.wireOp",EDGE,"E5.sketch_text.stroke-373"),sQuery(id+"F3.wireOp",EDGE,"E5.sketch_text.stroke-374"),sQuery(id+"F3.wireOp",EDGE,"E5.sketch_text.stroke-375"),sQuery(id+"F3.wireOp",EDGE,"E5.sketch_text.stroke-376"),sQuery(id+"F3.wireOp",EDGE,"E5.sketch_text.stroke-377"),sQuery(id+"F3.wireOp",EDGE,"E5.sketch_text.stroke-378"),sQuery(id+"F3.wireOp",EDGE,"E5.sketch_text.stroke-379"),sQuery(id+"F3.wireOp",EDGE,"E5.sketch_text.stroke-380"),sQuery(id+"F3.wireOp",EDGE,"E5.sketch_text.stroke-381"),sQuery(id+"F3.wireOp",EDGE,"E5.sketch_text.stroke-382"),sQuery(id+"F3.wireOp",EDGE,"E5.sketch_text.stroke-383"),sQuery(id+"F3.wireOp",EDGE,"E5.sketch_text.stroke-384"),sQuery(id+"F3.wireOp",EDGE,"E5.sketch_text.stroke-385"),sQuery(id+"F3.wireOp",EDGE,"E5.sketch_text.stroke-386"),sQuery(id+"F3.wireOp",EDGE,"E5.sketch_text.stroke-387"),sQuery(id+"F3.wireOp",EDGE,"E5.sketch_text.stroke-388"),sQuery(id+"F3.wireOp",EDGE,"E5.sketch_text.stroke-389"),sQuery(id+"F3.wireOp",EDGE,"E5.sketch_text.stroke-390"),sQuery(id+"F3.wireOp",EDGE,"E5.sketch_text.stroke-391"),sQuery(id+"F3.wireOp",EDGE,"E5.sketch_text.stroke-392"),sQuery(id+"F3.wireOp",EDGE,"E5.sketch_text.stroke-393")])]});
            transform(context, id + "F5", {"entities" : qUnion([Q0, Q1, Q2, Q3, Q4, Q5, Q6, Q7, Q8, Q9, Q10, Q11, Q12, Q13, Q14, Q15, Q16, Q17, Q18, Q19, Q20, Q21, Q22, Q23, Q24, Q25, Q26]), "transformType" : TransformType.TRANSLATION_3D, "dx" : 35 * mm, "dy" : -15.6 * mm, "dz" : 25.4 * mm, "makeCopy" : false});
        }
        {
            var Q0;
            {var subQ0=sQuery(id+"F0.wireOp",EDGE,"E4.bottom");var subQ1=sQuery(id+"F0.wireOp",EDGE,"E4.right");var subQ2=makeQuery(id+"F2.opExtrude","CAP_FACE",FACE,{"disambiguationData":[OSD([subQ0,sQuery(id+"F0.wireOp",EDGE,"E4.top"),sQuery(id+"F0.wireOp",EDGE,"E4.left"),subQ1])],"isStart":false});Q0=makeQuery(id+"F2.boolean.opBoolean","SPLIT",FACE,{"disambiguationData":[TD([makeQuery(id+"F1.opExtrude","SWEPT_FACE",FACE,{"disambiguationData":[OSD([sQuery(id+"F0.wireOp",EDGE,"E0")])]}),makeQuery(id+"F1.opExtrude","SWEPT_FACE",FACE,{"disambiguationData":[OSD([sQuery(id+"F0.wireOp",EDGE,"E1")])]}),makeQuery(id+"F1.opExtrude","SWEPT_FACE",FACE,{"disambiguationData":[OSD([sQuery(id+"F0.wireOp",EDGE,"E2")])]}),makeQuery(id+"F2.opExtrude","SWEPT_FACE",FACE,{"disambiguationData":[OSD([subQ0])]}),subQ2,makeQuery(id+"F2.opExtrude","SWEPT_FACE",FACE,{"disambiguationData":[OSD([subQ1])]})])],"derivedFrom":subQ2});}
            var sketch = newSketch(context, id + "F6", { "sketchPlane" : qUnion([Q0])});
            skArc(sketch, "E6", {"start": v(24.12, 41.48) * mm, "mid": v(13.03, 28.97) * mm, "end": v(24.12, 16.47) * mm});
            skFitSpline(sketch, "E7", {"points": [v(24.12, 41.48) * mm, v(24.12, 16.47) * mm], "startDerivative": vector(-18.53, -27.36) * mm, "endDerivative": vector(18.53, -17.65) * mm});
            skSolve(sketch);
        }
        {
            var Q0;
            Q0 = qSketchRegion(id + "F6", true);
            extrude(context, id + "F7", {"entities" : qUnion([Q0]), "operationType" : NewBodyOperationType.ADD, "depth" : 25.4 * mm});
        }
    });
